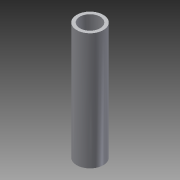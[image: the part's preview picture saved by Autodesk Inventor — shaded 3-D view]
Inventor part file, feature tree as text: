
AUTODESK INVENTOR PART (.ipt)
format: ipt  version: 2015 (Build 190159000, 159)  size: 92,160 bytes
history: native  units: in
note: dims shown in document units (in); Inventor stores cm internally (conversion verified against a paired STEP export)
features: extrude x1, sketch x1
ambient origin geometry x8: Origin, YZ Plane, XZ Plane, XY Plane, X Axis, Y Axis, Z Axis, Center Point
bodies: Solid1 (feature_tree)
feature tree (2):
  extrude  "Extrusion1"  Depth=2.75in
  sketch  "Sketch1"  dims[d0=0.625in d1=0.476in d2=2.75in d3=0.0in]
